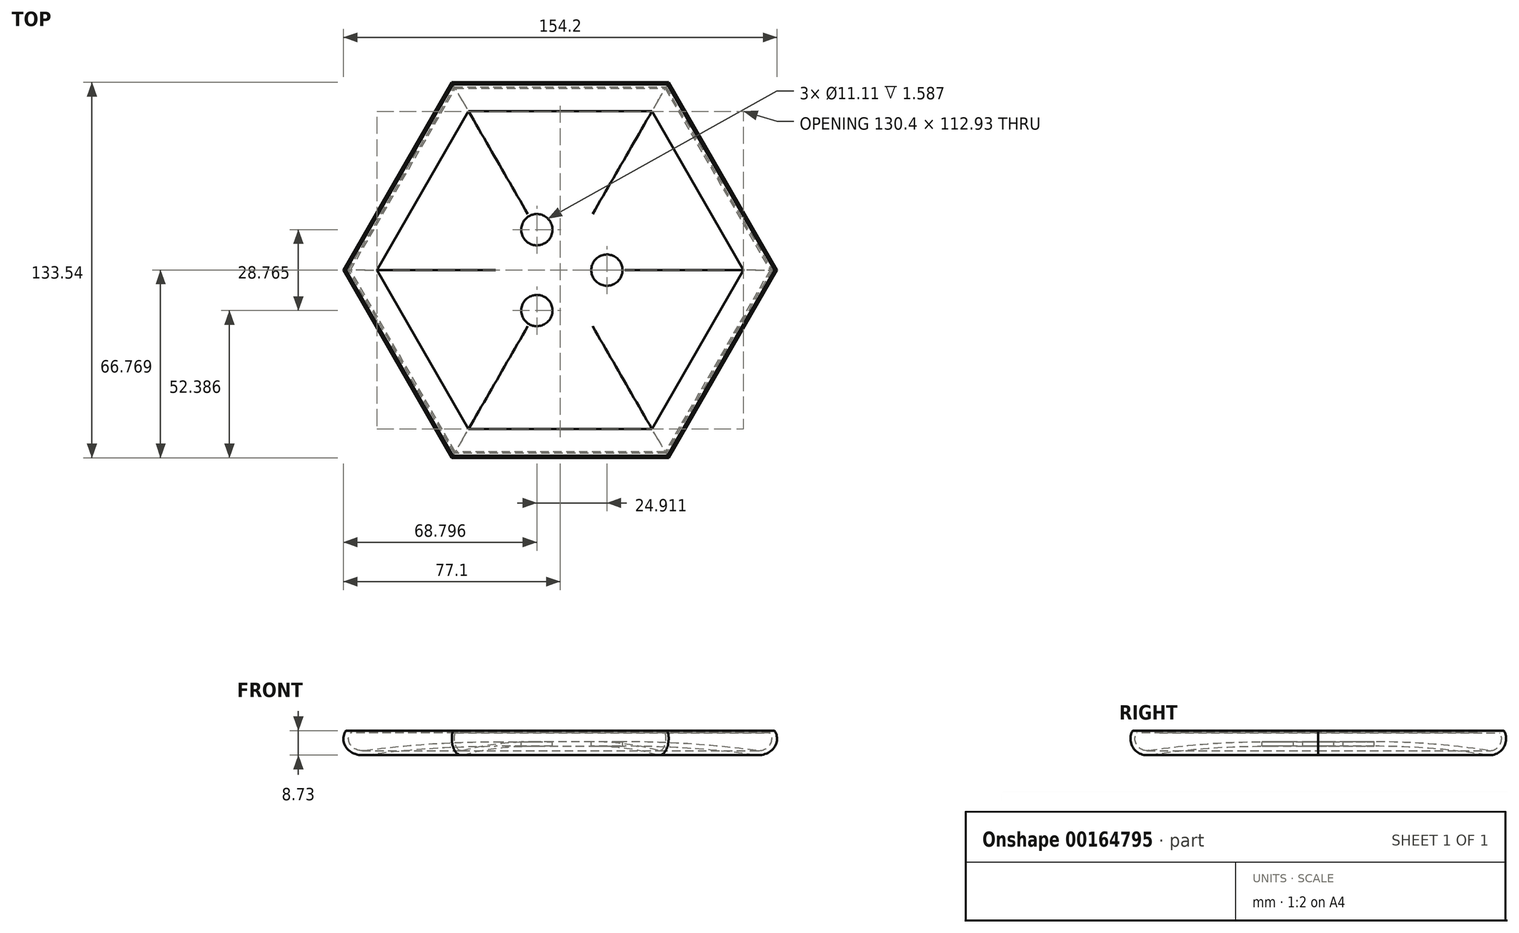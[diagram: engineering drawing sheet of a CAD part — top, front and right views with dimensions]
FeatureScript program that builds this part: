
annotation { "Feature Type Name" : "Feature", "Feature Type Description" : "" }
export const myFeature = defineFeature(function(context is Context, id is Id, definition is map)
    precondition{}
    {
        {
            var Q0;
            Q0=qCreatedBy(makeId("Top.planeOp"),FACE);
            var sketch = newSketch(context, id + "F0", { "sketchPlane" : qUnion([Q0])});
            skCircle(sketch, "E0.cCircle", {"center": v(38.1, -66) * mm, "radius": 66 * mm, "construction": true});
            skLineSegment(sketch, "E0.0", {"start": v(0, 0) * mm, "end": v(76.2, 0) * mm});
            skLineSegment(sketch, "E0.1", {"start": v(76.2, 0) * mm, "end": v(114.3, -66) * mm});
            skLineSegment(sketch, "E0.2", {"start": v(114.3, -66) * mm, "end": v(76.2, -131.98) * mm});
            skLineSegment(sketch, "E0.3", {"start": v(76.2, -131.98) * mm, "end": v(0, -131.98) * mm});
            skLineSegment(sketch, "E0.4", {"start": v(0, -131.98) * mm, "end": v(-38.1, -66) * mm});
            skLineSegment(sketch, "E0.5", {"start": v(-38.1, -66) * mm, "end": v(0, 0) * mm});
            skPoint(sketch, "E0.0.midPoint", {"position": v(38.1, 0) * mm});
            skSolve(sketch);
        }
        {
            var Q0;
            Q0 = qSketchRegion(id + "F0", true);
            extrude(context, id + "F1", {"entities" : qUnion([Q0]), "depth" : 0.8 * mm});
        }
        {
            var Q0;
            Q0=qCreatedBy(makeId("Right.planeOp"),FACE);
            var sketch = newSketch(context, id + "F2", { "sketchPlane" : qUnion([Q0])});
            skArc(sketch, "E1", {"start": v(-5.94, -7.87) * mm, "mid": v(-0.24, -5.4) * mm, "end": v(0, 0.8) * mm});
            skArc(sketch, "E2", {"start": v(-5.7, -6.3) * mm, "mid": v(-1.55, -4.5) * mm, "end": v(-1.37, 0) * mm});
            skLineSegment(sketch, "E3", {"start": v(0, 0.8) * mm, "end": v(-25.4, 0.8) * mm, "construction": true});
            skLineSegment(sketch, "E4", {"start": v(-25.4, 0.8) * mm, "end": v(-25.4, 44.79) * mm, "construction": true});
            skLineSegment(sketch, "E5", {"start": v(-25.4, 44.79) * mm, "end": v(0, 0.8) * mm, "construction": true});
            skLineSegment(sketch, "E6", {"start": v(0, 0.8) * mm, "end": v(0, 0) * mm});
            skLineSegment(sketch, "E7", {"start": v(0, 0) * mm, "end": v(-1.37, 0) * mm});
            skLineSegment(sketch, "E8", {"start": v(-5.94, -7.87) * mm, "end": v(-5.7, -6.3) * mm, "construction": true});
            skLineSegment(sketch, "E9", {"start": v(-5.04, -2.12) * mm, "end": v(-5.7, -6.3) * mm, "construction": true});
            skLineSegment(sketch, "E10", {"start": v(-66, 0) * mm, "end": v(-66, -3.17) * mm, "construction": true});
            skLineSegment(sketch, "E11", {"start": v(-66, -3.17) * mm, "end": v(-46.05, -3.17) * mm});
            skLineSegment(sketch, "E12", {"start": v(-66, -3.17) * mm, "end": v(-66, -4.76) * mm});
            skLineSegment(sketch, "E13", {"start": v(-66, -4.76) * mm, "end": v(-46.05, -4.76) * mm});
            skLineSegment(sketch, "E14", {"start": v(-46.05, -4.76) * mm, "end": v(-46.05, -3.17) * mm, "construction": true});
            skArc(sketch, "E15", {"start": v(-5.7, -6.3) * mm, "mid": v(-25.81, -3.96) * mm, "end": v(-46.05, -3.17) * mm});
            skArc(sketch, "E16", {"start": v(-5.94, -7.87) * mm, "mid": v(-25.93, -5.54) * mm, "end": v(-46.05, -4.76) * mm});
            skLineSegment(sketch, "E17", {"start": v(-66, -4.76) * mm, "end": v(-66, -7.94) * mm, "construction": true});
            skLineSegment(sketch, "E18", {"start": v(-66, -7.94) * mm, "end": v(-5.04, -7.94) * mm, "construction": true});
            skSolve(sketch);
        }
        {
            var Q0;
            Q0=makeQuery(id+"F2.imprint","IMPRINT",FACE,{"disambiguationData":[TD([[makeQuery(id+"F2.imprint","IMPRINT",EDGE,{"derivedFrom":sQuery(id+"F2.wireOp",EDGE,"E1")}),1.0]])]});
            var Q1;
            Q1=makeQuery(id+"F1.opExtrude","CAP_EDGE",EDGE,{"disambiguationData":[OSD([sQuery(id+"F0.wireOp",EDGE,"E0.0")])],"isStart":false});
            var Q2;
            Q2=makeQuery(id+"F1.opExtrude","CAP_EDGE",EDGE,{"disambiguationData":[OSD([sQuery(id+"F0.wireOp",EDGE,"E0.1")])],"isStart":false});
            var Q3;
            Q3=makeQuery(id+"F1.opExtrude","CAP_EDGE",EDGE,{"disambiguationData":[OSD([sQuery(id+"F0.wireOp",EDGE,"E0.2")])],"isStart":false});
            var Q4;
            Q4=makeQuery(id+"F1.opExtrude","CAP_EDGE",EDGE,{"disambiguationData":[OSD([sQuery(id+"F0.wireOp",EDGE,"E0.3")])],"isStart":false});
            var Q5;
            Q5=makeQuery(id+"F1.opExtrude","CAP_EDGE",EDGE,{"disambiguationData":[OSD([sQuery(id+"F0.wireOp",EDGE,"E0.4")])],"isStart":false});
            var Q6;
            Q6=makeQuery(id+"F1.opExtrude","CAP_EDGE",EDGE,{"disambiguationData":[OSD([sQuery(id+"F0.wireOp",EDGE,"E0.5")])],"isStart":false});
            sweep(context, id + "F3", {"operationType" : NewBodyOperationType.ADD, "profiles" : qUnion([Q0]), "path" : qUnion([Q1, Q2, Q3, Q4, Q5, Q6])});
        }
        {
            var Q0;
            Q0=makeQuery(id+"F1.opExtrude","CAP_FACE",FACE,{"disambiguationData":[OSD([sQuery(id+"F0.wireOp",EDGE,"E0.0"),sQuery(id+"F0.wireOp",EDGE,"E0.1"),sQuery(id+"F0.wireOp",EDGE,"E0.2"),sQuery(id+"F0.wireOp",EDGE,"E0.3"),sQuery(id+"F0.wireOp",EDGE,"E0.4"),sQuery(id+"F0.wireOp",EDGE,"E0.5")])],"isStart":false});
            var sketch = newSketch(context, id + "F4", { "sketchPlane" : qUnion([Q0])});
            skCircle(sketch, "E19.cCircle", {"center": v(38.1, -66) * mm, "radius": 56.47 * mm, "construction": true});
            skLineSegment(sketch, "E19.0", {"start": v(5.5, -122.46) * mm, "end": v(-27.1, -66) * mm});
            skLineSegment(sketch, "E19.1", {"start": v(-27.1, -66) * mm, "end": v(5.5, -9.53) * mm});
            skLineSegment(sketch, "E19.2", {"start": v(5.5, -9.53) * mm, "end": v(70.7, -9.53) * mm});
            skLineSegment(sketch, "E19.3", {"start": v(70.7, -9.53) * mm, "end": v(103.3, -66) * mm});
            skLineSegment(sketch, "E19.4", {"start": v(103.3, -66) * mm, "end": v(70.7, -122.46) * mm});
            skLineSegment(sketch, "E19.5", {"start": v(70.7, -122.46) * mm, "end": v(5.5, -122.46) * mm});
            skPoint(sketch, "E19.0.midPoint", {"position": v(-10.8, -94.22) * mm});
            skLineSegment(sketch, "E20", {"start": v(76.2, 0) * mm, "end": v(0, -131.98) * mm, "construction": true});
            skLineSegment(sketch, "E21", {"start": v(-10.8, -37.76) * mm, "end": v(-19.05, -33) * mm, "construction": true});
            skSolve(sketch);
        }
        {
            var Q0;
            Q0 = qSketchRegion(id + "F4", true);
            extrude(context, id + "F5", {"entities" : qUnion([Q0]), "operationType" : NewBodyOperationType.REMOVE, "oppositeDirection" : true, "depth" : 1.59 * mm});
        }
        {
            var Q0;
            Q0=makeQuery(id+"F3.opSweep","SWEPT_FACE",FACE,{"disambiguationData":[OSD([sQuery(id+"F0.wireOp",EDGE,"E0.0"),sQuery(id+"F2.wireOp",EDGE,"E11")])]});
            var sketch = newSketch(context, id + "F6", { "sketchPlane" : qUnion([Q0])});
            skCircle(sketch, "E22.cCircle", {"center": v(38.1, -66) * mm, "radius": 8.3 * mm, "construction": true});
            skLineSegment(sketch, "E22.0", {"start": v(54.7, -66) * mm, "end": v(29.8, -80.37) * mm, "construction": true});
            skLineSegment(sketch, "E22.1", {"start": v(29.8, -80.37) * mm, "end": v(29.8, -51.6) * mm, "construction": true});
            skLineSegment(sketch, "E22.2", {"start": v(29.8, -51.6) * mm, "end": v(54.7, -66) * mm, "construction": true});
            skPoint(sketch, "E22.0.midPoint", {"position": v(42.25, -73.18) * mm});
            skCircle(sketch, "E23", {"center": v(29.8, -51.6) * mm, "radius": 5.56 * mm});
            skLineSegment(sketch, "E24", {"start": v(61.12, -66) * mm, "end": v(15.08, -66) * mm, "construction": true});
            skCircle(sketch, "E25", {"center": v(54.7, -66) * mm, "radius": 5.56 * mm});
            skCircle(sketch, "E26", {"center": v(29.8, -80.37) * mm, "radius": 5.56 * mm});
            skSolve(sketch);
        }
        {
            var Q0;
            Q0 = qSketchRegion(id + "F6", true);
            extrude(context, id + "F7", {"entities" : qUnion([Q0]), "operationType" : NewBodyOperationType.REMOVE, "endBound" : BoundingType.THROUGH_ALL, "oppositeDirection" : true, "depth" : 25.4 * mm});
        }
    });
